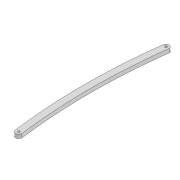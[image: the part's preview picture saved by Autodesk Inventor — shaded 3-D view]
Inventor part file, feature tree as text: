
AUTODESK INVENTOR PART (.ipt)
format: ipt  version: 2022 (Build 260153000, 153)  size: 94,720 bytes
history: native  units: mm
features: extrude x1, sketch x1
ambient origin geometry x8: Origin, YZ Plane, XZ Plane, XY Plane, X Axis, Y Axis, Z Axis, Center Point
bodies: Solid1 (feature_tree)
feature tree (2):
  extrude  "Extrusion1"  Depth=900.0mm
  sketch  "Sketch1"  dims[d0=3.3mm d1=3.3mm d2=10.0mm d3=230.652mm d6=6.0mm d7=0.0mm d14=900.0mm d15=900.0mm]
